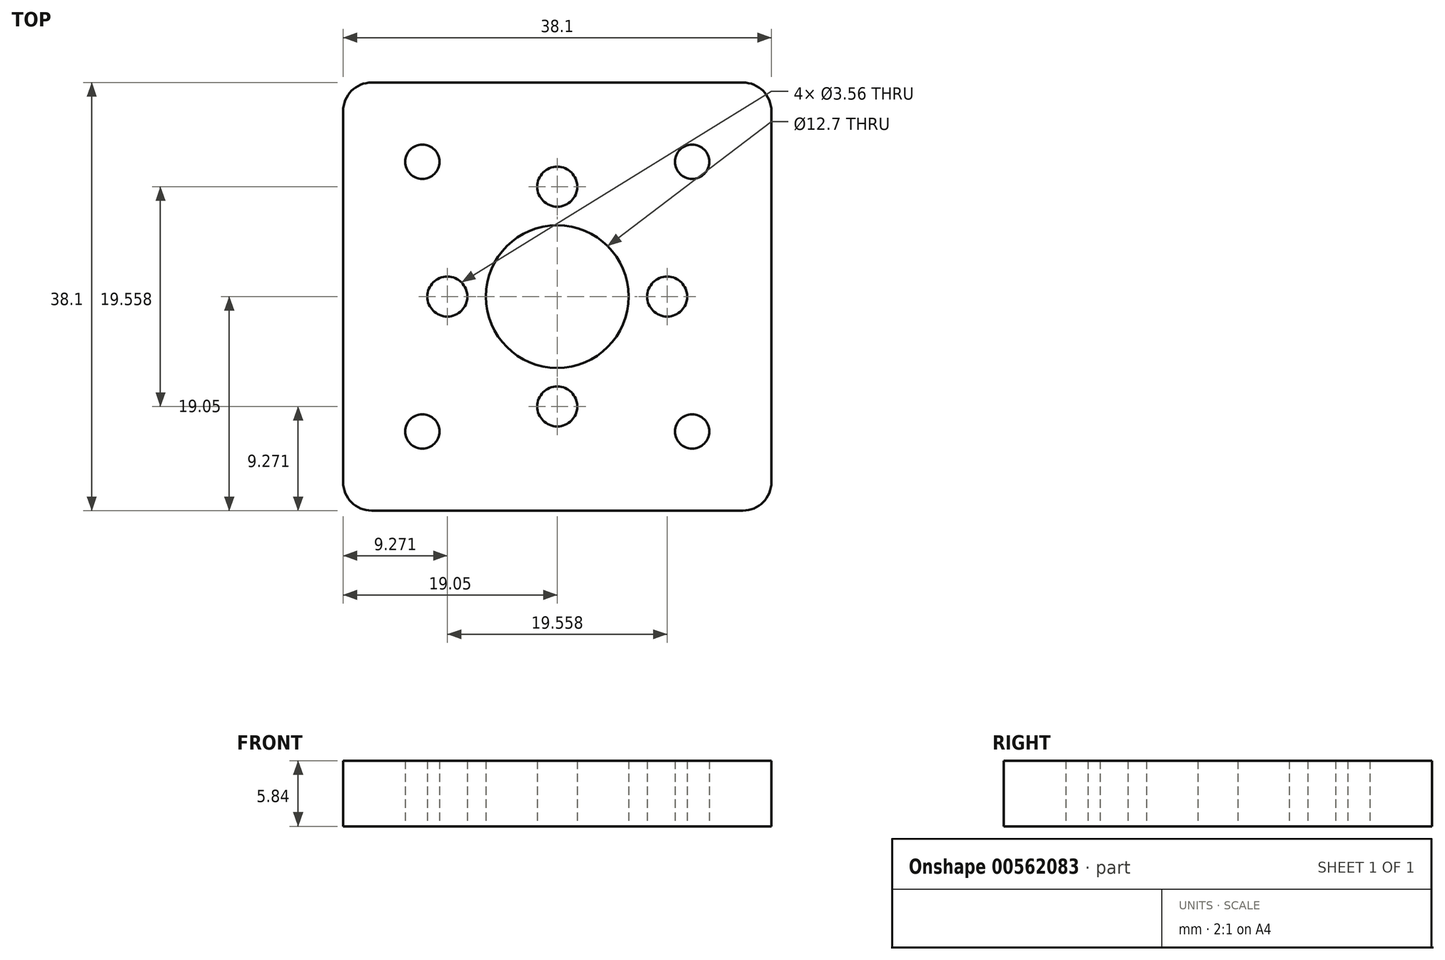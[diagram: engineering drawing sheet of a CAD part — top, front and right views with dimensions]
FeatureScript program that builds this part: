
annotation { "Feature Type Name" : "Feature", "Feature Type Description" : "" }
export const myFeature = defineFeature(function(context is Context, id is Id, definition is map)
    precondition{}
    {
        {
            var Q0;
            Q0=qCreatedBy(makeId("Top.planeOp"),FACE);
            var sketch = newSketch(context, id + "F0", { "sketchPlane" : qUnion([Q0])});
            skCircle(sketch, "E0", {"center": v(0, 0) * mm, "radius": 6.35 * mm});
            skCircle(sketch, "E1", {"center": v(-12, -12) * mm, "radius": 1.52 * mm});
            skCircle(sketch, "E2", {"center": v(12, -12) * mm, "radius": 1.52 * mm});
            skCircle(sketch, "E3", {"center": v(12, 12) * mm, "radius": 1.52 * mm});
            skCircle(sketch, "E4", {"center": v(-12, 12) * mm, "radius": 1.52 * mm});
            skCircle(sketch, "E5", {"center": v(9.78, 0) * mm, "radius": 1.78 * mm});
            skCircle(sketch, "E6", {"center": v(0, -9.78) * mm, "radius": 1.78 * mm});
            skCircle(sketch, "E7", {"center": v(-9.78, 0) * mm, "radius": 1.78 * mm});
            skCircle(sketch, "E8", {"center": v(0, 9.78) * mm, "radius": 1.78 * mm});
            skLineSegment(sketch, "E9.bottom", {"start": v(-16.51, 19.05) * mm, "end": v(16.51, 19.05) * mm});
            skLineSegment(sketch, "E9.top", {"start": v(-16.51, -19.05) * mm, "end": v(16.51, -19.05) * mm});
            skLineSegment(sketch, "E9.left", {"start": v(-19.05, 16.51) * mm, "end": v(-19.05, -16.5) * mm});
            skLineSegment(sketch, "E9.right", {"start": v(19.05, 16.51) * mm, "end": v(19.05, -16.5) * mm});
            skPoint(sketch, "E10.visualSharp", {"position": v(-19.05, 19.05) * mm});
            skArc(sketch, "E10.filletArc", {"start": v(-16.51, 19.05) * mm, "mid": v(-18.3, 18.3) * mm, "end": v(-19.05, 16.51) * mm});
            skPoint(sketch, "E11.visualSharp", {"position": v(19.05, 19.05) * mm});
            skArc(sketch, "E11.filletArc", {"start": v(19.05, 16.51) * mm, "mid": v(18.3, 18.3) * mm, "end": v(16.51, 19.05) * mm});
            skPoint(sketch, "E12.visualSharp", {"position": v(19.05, -19.05) * mm});
            skArc(sketch, "E12.filletArc", {"start": v(16.51, -19.05) * mm, "mid": v(18.3, -18.3) * mm, "end": v(19.05, -16.5) * mm});
            skPoint(sketch, "E13.visualSharp", {"position": v(-19.05, -19.05) * mm});
            skArc(sketch, "E13.filletArc", {"start": v(-19.05, -16.5) * mm, "mid": v(-18.3, -18.3) * mm, "end": v(-16.51, -19.05) * mm});
            skSolve(sketch);
        }
        {
            var Q0;
            Q0 = qSketchRegion(id + "F0", true);
            extrude(context, id + "F1", {"entities" : qUnion([Q0]), "depth" : 5.84 * mm, "offsetDistance" : 25.4 * mm});
        }
    });
